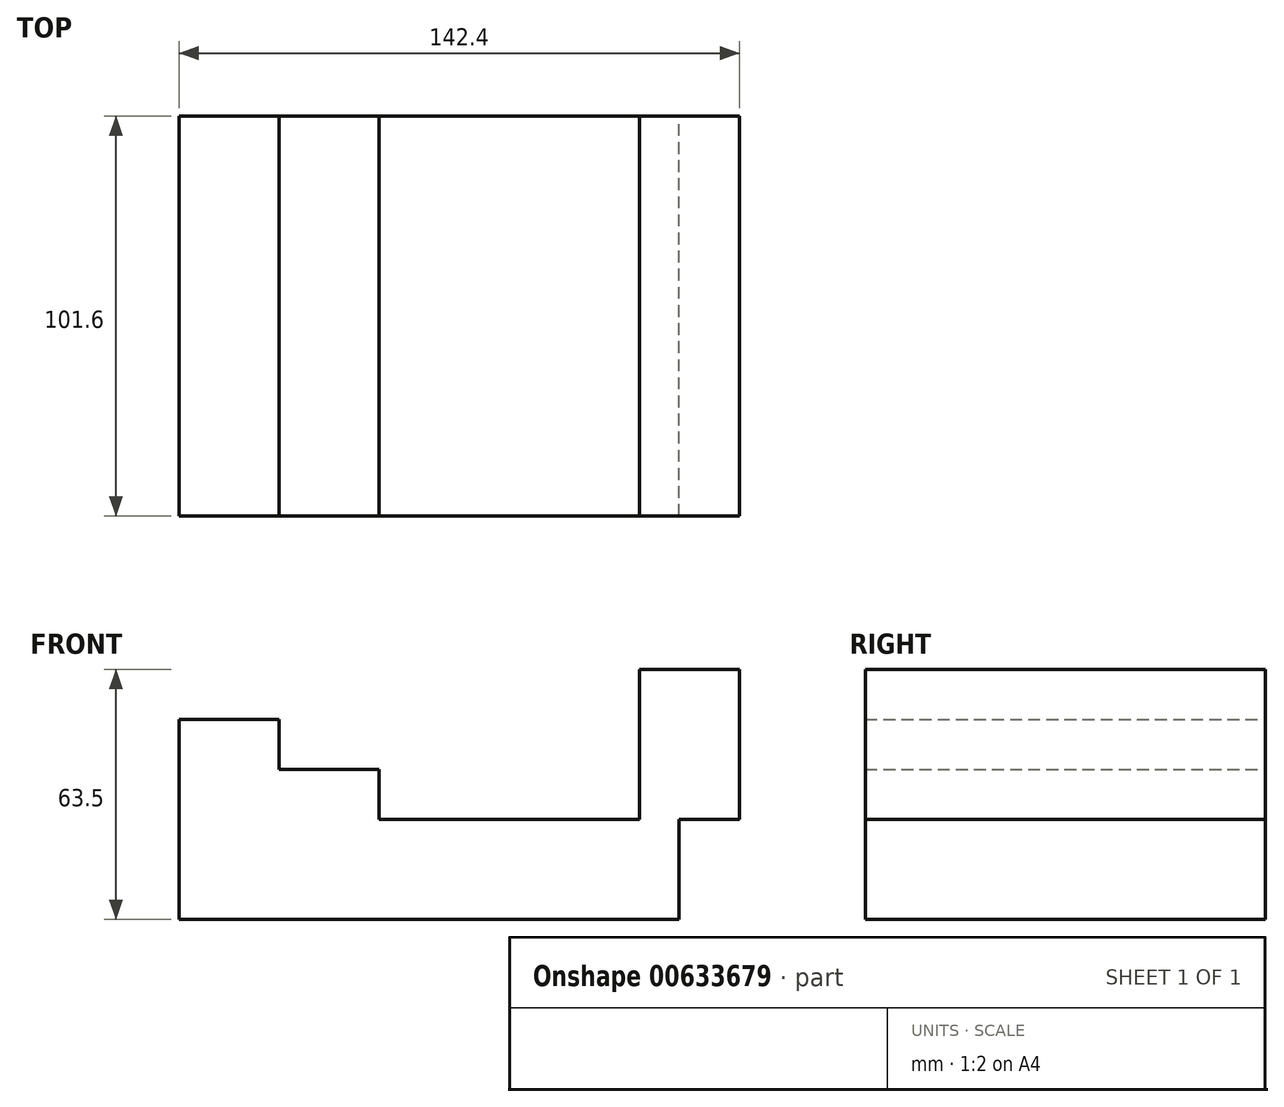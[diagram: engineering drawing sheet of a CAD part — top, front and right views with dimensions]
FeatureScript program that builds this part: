
annotation { "Feature Type Name" : "Feature", "Feature Type Description" : "" }
export const myFeature = defineFeature(function(context is Context, id is Id, definition is map)
    precondition{}
    {
        {
            var Q0;
            Q0=qCreatedBy(makeId("Front.planeOp"),FACE);
            var sketch = newSketch(context, id + "F0", { "sketchPlane" : qUnion([Q0])});
            skLineSegment(sketch, "E0", {"start": v(121.02, 0) * mm, "end": v(248.02, 0) * mm});
            skLineSegment(sketch, "E1", {"start": v(248.02, 0) * mm, "end": v(248.02, 25.4) * mm});
            skLineSegment(sketch, "E2", {"start": v(248.02, 25.4) * mm, "end": v(263.42, 25.4) * mm});
            skLineSegment(sketch, "E3", {"start": v(263.42, 25.4) * mm, "end": v(263.42, 63.5) * mm});
            skLineSegment(sketch, "E4", {"start": v(121.02, 0) * mm, "end": v(121.02, 50.8) * mm});
            skLineSegment(sketch, "E5", {"start": v(121.02, 50.8) * mm, "end": v(146.42, 50.8) * mm});
            skLineSegment(sketch, "E6", {"start": v(146.42, 50.8) * mm, "end": v(146.42, 25.4) * mm});
            skLineSegment(sketch, "E7", {"start": v(263.42, 63.5) * mm, "end": v(238.02, 63.5) * mm});
            skLineSegment(sketch, "E8", {"start": v(146.42, 25.4) * mm, "end": v(216.69, 25.4) * mm});
            skLineSegment(sketch, "E9", {"start": v(238.02, 63.5) * mm, "end": v(238.02, 25.4) * mm});
            skLineSegment(sketch, "E10", {"start": v(238.02, 25.4) * mm, "end": v(216.69, 25.4) * mm});
            skLineSegment(sketch, "E11", {"start": v(146.42, 38.1) * mm, "end": v(171.82, 38.1) * mm});
            skLineSegment(sketch, "E12", {"start": v(171.82, 38.1) * mm, "end": v(171.82, 25.4) * mm});
            skLineSegment(sketch, "E13", {"start": v(181.55, 25.4) * mm, "end": v(189.02, 82.3) * mm});
            skLineSegment(sketch, "E14", {"start": v(189.02, 82.3) * mm, "end": v(189.02, 101.24) * mm});
            skLineSegment(sketch, "E15", {"start": v(189.02, 101.24) * mm, "end": v(205.6, 108.63) * mm});
            skSolve(sketch);
        }
        {
            var Q0;
            Q0 = qSketchRegion(id + "F0", true);
            extrude(context, id + "F1", {"entities" : qUnion([Q0]), "depth" : 101.6 * mm, "offsetDistance" : 25.4 * mm});
        }
        {
            var Q0;
            Q0 = qSketchRegion(id + "F0", true);
            extrude(context, id + "F2", {"entities" : qUnion([Q0]), "operationType" : NewBodyOperationType.ADD, "depth" : 25.4 * mm, "offsetDistance" : 25.4 * mm});
        }
    });
